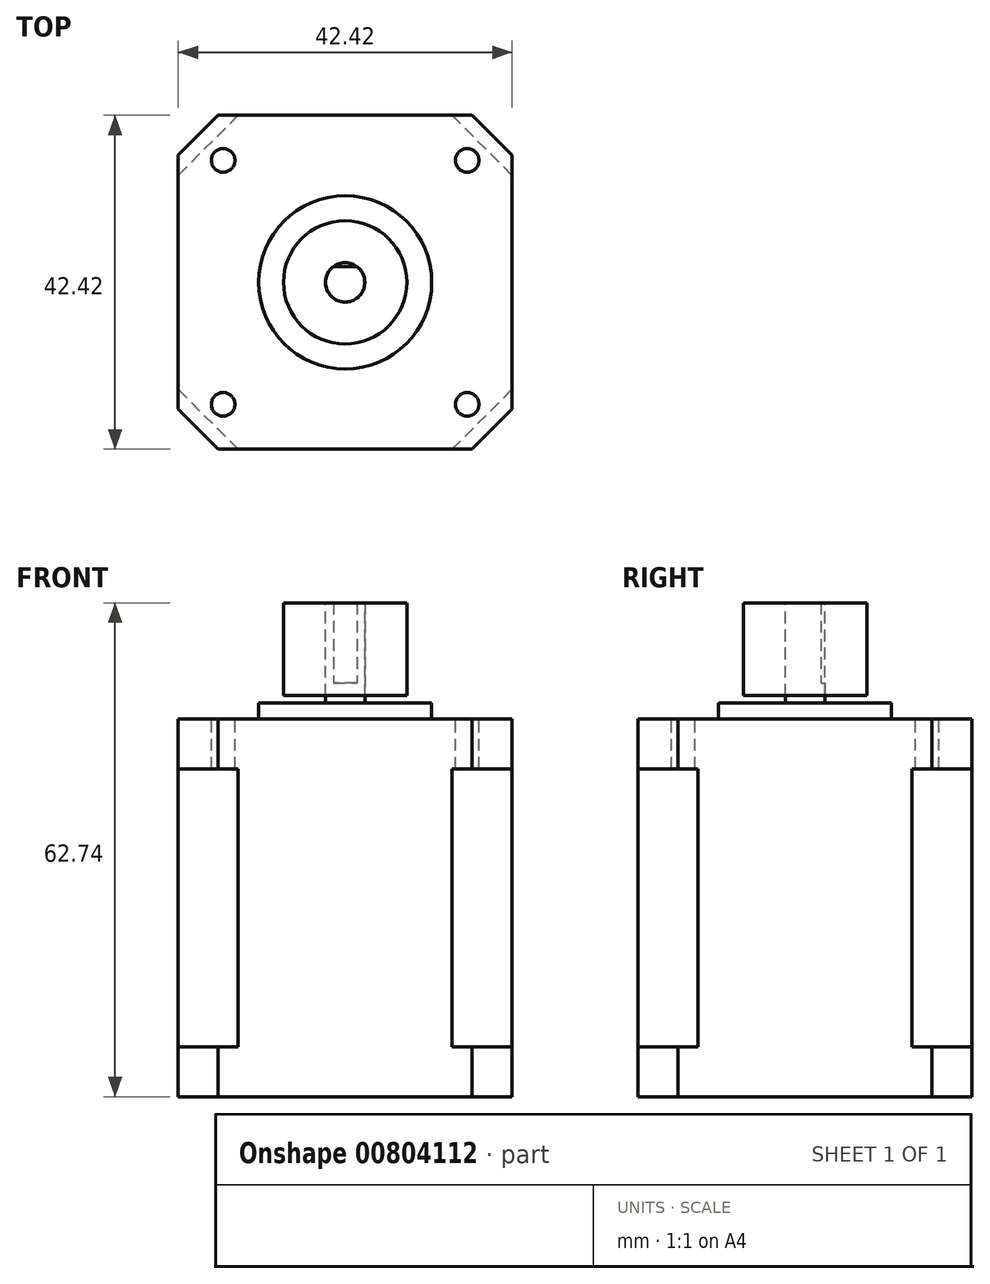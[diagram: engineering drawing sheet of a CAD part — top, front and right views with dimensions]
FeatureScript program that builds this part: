
annotation { "Feature Type Name" : "Feature", "Feature Type Description" : "" }
export const myFeature = defineFeature(function(context is Context, id is Id, definition is map)
    precondition{}
    {
        {
            var Q0;
            Q0=qCreatedBy(makeId("Top.planeOp"),FACE);
            var sketch = newSketch(context, id + "F0", { "sketchPlane" : qUnion([Q0]), "asVersion" : FeatureScriptVersionNumber.V236_DEFAULT_MAX_ASSEMBLIES});
            skLineSegment(sketch, "E0.bottom", {"start": v(-21.2, 21.2) * mm, "end": v(21.2, 21.2) * mm});
            skLineSegment(sketch, "E0.top", {"start": v(-21.2, -21.2) * mm, "end": v(21.2, -21.2) * mm});
            skLineSegment(sketch, "E0.left", {"start": v(-21.2, 21.2) * mm, "end": v(-21.2, -21.2) * mm});
            skLineSegment(sketch, "E0.right", {"start": v(21.2, 21.2) * mm, "end": v(21.2, -21.2) * mm});
            skSolve(sketch);
        }
        {
            var Q0;
            Q0=makeQuery(id+"F0.imprint","IMPRINT",FACE,{"disambiguationData":[TD([[makeQuery(id+"F0.imprint","IMPRINT",EDGE,{"derivedFrom":sQuery(id+"F0.wireOp",EDGE,"E0.bottom")}),-1.0]])]});
            extrude(context, id + "F1", {"entities" : qUnion([Q0]), "endBound" : BoundingType.SYMMETRIC, "depth" : 35.3 * mm});
        }
        {
            var Q0;
            Q0=makeQuery(id+"F1.opExtrude","SWEPT_EDGE",EDGE,{"disambiguationData":[OSD([sQuery(id+"F0.wireOp",EDGE,"E0.bottom"),sQuery(id+"F0.wireOp",EDGE,"E0.right")])]});
            var Q1;
            Q1=makeQuery(id+"F1.opExtrude","SWEPT_EDGE",EDGE,{"disambiguationData":[OSD([sQuery(id+"F0.wireOp",EDGE,"E0.bottom"),sQuery(id+"F0.wireOp",EDGE,"E0.left")])]});
            var Q2;
            Q2=makeQuery(id+"F1.opExtrude","SWEPT_EDGE",EDGE,{"disambiguationData":[OSD([sQuery(id+"F0.wireOp",EDGE,"E0.top"),sQuery(id+"F0.wireOp",EDGE,"E0.left")])]});
            var Q3;
            Q3=makeQuery(id+"F1.opExtrude","SWEPT_EDGE",EDGE,{"disambiguationData":[OSD([sQuery(id+"F0.wireOp",EDGE,"E0.top"),sQuery(id+"F0.wireOp",EDGE,"E0.right")])]});
            chamfer(context, id + "F2", {"entities" : qUnion([Q0, Q1, Q2, Q3]), "width" : 7.62 * mm, "tangentPropagation" : true});
        }
        {
            var Q0;
            Q0=makeQuery(id+"F1.opExtrude","CAP_FACE",FACE,{"disambiguationData":[OSD([sQuery(id+"F0.wireOp",EDGE,"E0.bottom"),sQuery(id+"F0.wireOp",EDGE,"E0.top"),sQuery(id+"F0.wireOp",EDGE,"E0.left"),sQuery(id+"F0.wireOp",EDGE,"E0.right")])],"isStart":false});
            var sketch = newSketch(context, id + "F3", { "sketchPlane" : qUnion([Q0]), "asVersion" : FeatureScriptVersionNumber.V236_DEFAULT_MAX_ASSEMBLIES});
            skLineSegment(sketch, "E1.bottom", {"start": v(-21.2, 21.2) * mm, "end": v(21.2, 21.2) * mm});
            skLineSegment(sketch, "E1.top", {"start": v(-21.2, -21.2) * mm, "end": v(21.2, -21.2) * mm});
            skLineSegment(sketch, "E1.left", {"start": v(-21.2, 21.2) * mm, "end": v(-21.2, -21.2) * mm});
            skLineSegment(sketch, "E1.right", {"start": v(21.2, 21.2) * mm, "end": v(21.2, -21.2) * mm});
            skSolve(sketch);
        }
        {
            var Q0;
            {var subQ0=sQuery(id+"F0.wireOp",EDGE,"E0.top");var subQ1=sQuery(id+"F0.wireOp",EDGE,"E0.right");var subQ2=sQuery(id+"F0.wireOp",EDGE,"E0.bottom");var subQ3=sQuery(id+"F0.wireOp",EDGE,"E0.left");var subQ4=makeQuery(id+"F1.opExtrude","CAP_FACE",FACE,{"disambiguationData":[OSD([subQ2,subQ0,subQ3,subQ1])],"isStart":false});var subQ8=makeQuery(id+"F2.opChamfer","BLEND_EDGE",EDGE,{"blendedFrom":[makeQuery(id+"F1.opExtrude","SWEPT_EDGE",EDGE,{"disambiguationData":[OSD([subQ2,subQ3])]}),subQ4],"blendedInto":[subQ4]});Q0=makeQuery(id+"F3.imprint","IMPRINT",FACE,{"disambiguationData":[TD([[makeQuery(id+"F3.imprint","IMPRINT",EDGE,{"derivedFrom":subQ8}),1.0]])]});}
            var Q1;
            {var subQ0=sQuery(id+"F0.wireOp",EDGE,"E0.bottom");var subQ1=sQuery(id+"F0.wireOp",EDGE,"E0.right");var subQ2=makeQuery(id+"F2.opChamfer","BLEND_EDGE",EDGE,{"blendedFrom":[makeQuery(id+"F1.opExtrude","SWEPT_EDGE",EDGE,{"disambiguationData":[OSD([subQ0,subQ1])]}),makeQuery(id+"F1.opExtrude","CAP_FACE",FACE,{"disambiguationData":[OSD([subQ0,sQuery(id+"F0.wireOp",EDGE,"E0.top"),sQuery(id+"F0.wireOp",EDGE,"E0.left"),subQ1])],"isStart":false})],"blendedInto":[makeQuery(id+"F1.opExtrude","CAP_FACE",FACE,{"disambiguationData":[OSD([subQ0,sQuery(id+"F0.wireOp",EDGE,"E0.top"),sQuery(id+"F0.wireOp",EDGE,"E0.left"),subQ1])],"isStart":false})]});Q1=makeQuery(id+"F3.imprint","IMPRINT",FACE,{"disambiguationData":[TD([[makeQuery(id+"F3.imprint","IMPRINT",EDGE,{"derivedFrom":subQ2}),-1.0]])]});}
            var Q2;
            {var subQ0=sQuery(id+"F0.wireOp",EDGE,"E0.bottom");var subQ1=sQuery(id+"F0.wireOp",EDGE,"E0.left");var subQ2=makeQuery(id+"F2.opChamfer","BLEND_EDGE",EDGE,{"blendedFrom":[makeQuery(id+"F1.opExtrude","SWEPT_EDGE",EDGE,{"disambiguationData":[OSD([subQ0,subQ1])]}),makeQuery(id+"F1.opExtrude","CAP_FACE",FACE,{"disambiguationData":[OSD([subQ0,sQuery(id+"F0.wireOp",EDGE,"E0.top"),subQ1,sQuery(id+"F0.wireOp",EDGE,"E0.right")])],"isStart":false})],"blendedInto":[makeQuery(id+"F1.opExtrude","CAP_FACE",FACE,{"disambiguationData":[OSD([subQ0,sQuery(id+"F0.wireOp",EDGE,"E0.top"),subQ1,sQuery(id+"F0.wireOp",EDGE,"E0.right")])],"isStart":false})]});Q2=makeQuery(id+"F3.imprint","IMPRINT",FACE,{"disambiguationData":[TD([[makeQuery(id+"F3.imprint","IMPRINT",EDGE,{"derivedFrom":subQ2}),-1.0]])]});}
            var Q3;
            {var subQ0=sQuery(id+"F0.wireOp",EDGE,"E0.top");var subQ1=sQuery(id+"F0.wireOp",EDGE,"E0.left");var subQ2=makeQuery(id+"F2.opChamfer","BLEND_EDGE",EDGE,{"blendedFrom":[makeQuery(id+"F1.opExtrude","SWEPT_EDGE",EDGE,{"disambiguationData":[OSD([subQ0,subQ1])]}),makeQuery(id+"F1.opExtrude","CAP_FACE",FACE,{"disambiguationData":[OSD([sQuery(id+"F0.wireOp",EDGE,"E0.bottom"),subQ0,subQ1,sQuery(id+"F0.wireOp",EDGE,"E0.right")])],"isStart":false})],"blendedInto":[makeQuery(id+"F1.opExtrude","CAP_FACE",FACE,{"disambiguationData":[OSD([sQuery(id+"F0.wireOp",EDGE,"E0.bottom"),subQ0,subQ1,sQuery(id+"F0.wireOp",EDGE,"E0.right")])],"isStart":false})]});Q3=makeQuery(id+"F3.imprint","IMPRINT",FACE,{"disambiguationData":[TD([[makeQuery(id+"F3.imprint","IMPRINT",EDGE,{"derivedFrom":subQ2}),-1.0]])]});}
            var Q4;
            {var subQ0=sQuery(id+"F0.wireOp",EDGE,"E0.top");var subQ1=sQuery(id+"F0.wireOp",EDGE,"E0.right");var subQ2=makeQuery(id+"F2.opChamfer","BLEND_EDGE",EDGE,{"blendedFrom":[makeQuery(id+"F1.opExtrude","SWEPT_EDGE",EDGE,{"disambiguationData":[OSD([subQ0,subQ1])]}),makeQuery(id+"F1.opExtrude","CAP_FACE",FACE,{"disambiguationData":[OSD([sQuery(id+"F0.wireOp",EDGE,"E0.bottom"),subQ0,sQuery(id+"F0.wireOp",EDGE,"E0.left"),subQ1])],"isStart":false})],"blendedInto":[makeQuery(id+"F1.opExtrude","CAP_FACE",FACE,{"disambiguationData":[OSD([sQuery(id+"F0.wireOp",EDGE,"E0.bottom"),subQ0,sQuery(id+"F0.wireOp",EDGE,"E0.left"),subQ1])],"isStart":false})]});Q4=makeQuery(id+"F3.imprint","IMPRINT",FACE,{"disambiguationData":[TD([[makeQuery(id+"F3.imprint","IMPRINT",EDGE,{"derivedFrom":subQ2}),-1.0]])]});}
            extrude(context, id + "F4", {"entities" : qUnion([Q0, Q1, Q2, Q3, Q4]), "operationType" : NewBodyOperationType.ADD, "depth" : 6.35 * mm});
        }
        {
            var Q0;
            Q0=makeQuery(id+"F4.opExtrude","SWEPT_EDGE",EDGE,{"disambiguationData":[OSD([sQuery(id+"F3.wireOp",EDGE,"E1.bottom"),sQuery(id+"F3.wireOp",EDGE,"E1.right")])]});
            var Q1;
            Q1=makeQuery(id+"F4.opExtrude","SWEPT_EDGE",EDGE,{"disambiguationData":[OSD([sQuery(id+"F3.wireOp",EDGE,"E1.bottom"),sQuery(id+"F3.wireOp",EDGE,"E1.left")])]});
            var Q2;
            Q2=makeQuery(id+"F4.opExtrude","SWEPT_EDGE",EDGE,{"disambiguationData":[OSD([sQuery(id+"F3.wireOp",EDGE,"E1.top"),sQuery(id+"F3.wireOp",EDGE,"E1.left")])]});
            var Q3;
            Q3=makeQuery(id+"F4.opExtrude","SWEPT_EDGE",EDGE,{"disambiguationData":[OSD([sQuery(id+"F3.wireOp",EDGE,"E1.top"),sQuery(id+"F3.wireOp",EDGE,"E1.right")])]});
            chamfer(context, id + "F5", {"entities" : qUnion([Q0, Q1, Q2, Q3]), "width" : 5.08 * mm, "tangentPropagation" : true});
        }
        {
            var Q0;
            Q0=makeQuery(id+"F1.opExtrude","CAP_FACE",FACE,{"disambiguationData":[OSD([sQuery(id+"F0.wireOp",EDGE,"E0.bottom"),sQuery(id+"F0.wireOp",EDGE,"E0.top"),sQuery(id+"F0.wireOp",EDGE,"E0.left"),sQuery(id+"F0.wireOp",EDGE,"E0.right")])],"isStart":true});
            var sketch = newSketch(context, id + "F6", { "sketchPlane" : qUnion([Q0]), "asVersion" : FeatureScriptVersionNumber.V236_DEFAULT_MAX_ASSEMBLIES});
            skLineSegment(sketch, "E2.0.0", {"start": v(-16.13, 21.2) * mm, "end": v(16.13, 21.2) * mm});
            skLineSegment(sketch, "E2.0.1", {"start": v(16.13, 21.2) * mm, "end": v(21.2, 16.13) * mm});
            skLineSegment(sketch, "E2.0.2", {"start": v(21.2, -16.13) * mm, "end": v(21.2, 16.13) * mm});
            skLineSegment(sketch, "E2.0.3", {"start": v(21.2, -16.13) * mm, "end": v(16.13, -21.2) * mm});
            skLineSegment(sketch, "E2.0.4", {"start": v(-16.13, -21.2) * mm, "end": v(16.13, -21.2) * mm});
            skLineSegment(sketch, "E2.0.5", {"start": v(-16.13, -21.2) * mm, "end": v(-21.2, -16.13) * mm});
            skLineSegment(sketch, "E2.0.6", {"start": v(-21.2, -16.13) * mm, "end": v(-21.2, 16.13) * mm});
            skLineSegment(sketch, "E2.0.7", {"start": v(-21.2, 16.13) * mm, "end": v(-16.13, 21.2) * mm});
            skSolve(sketch);
        }
        {
            var Q0;
            {var subQ3=sQuery(id+"F6.wireOp",EDGE,"E2.0.7");Q0=makeQuery(id+"F6.imprint","IMPRINT",FACE,{"disambiguationData":[TD([[makeQuery(id+"F6.imprint","IMPRINT",EDGE,{"derivedFrom":subQ3}),-1.0]])]});}
            var Q1;
            {var subQ4=sQuery(id+"F6.wireOp",EDGE,"E2.0.1");Q1=makeQuery(id+"F6.imprint","IMPRINT",FACE,{"disambiguationData":[TD([[makeQuery(id+"F6.imprint","IMPRINT",EDGE,{"derivedFrom":subQ4}),-1.0]])]});}
            var Q2;
            {var subQ4=sQuery(id+"F6.wireOp",EDGE,"E2.0.3");Q2=makeQuery(id+"F6.imprint","IMPRINT",FACE,{"disambiguationData":[TD([[makeQuery(id+"F6.imprint","IMPRINT",EDGE,{"derivedFrom":subQ4}),-1.0]])]});}
            var Q3;
            {var subQ4=sQuery(id+"F6.wireOp",EDGE,"E2.0.5");Q3=makeQuery(id+"F6.imprint","IMPRINT",FACE,{"disambiguationData":[TD([[makeQuery(id+"F6.imprint","IMPRINT",EDGE,{"derivedFrom":subQ4}),-1.0]])]});}
            var Q4;
            {var subQ0=sQuery(id+"F0.wireOp",EDGE,"E0.top");var subQ1=sQuery(id+"F0.wireOp",EDGE,"E0.right");var subQ2=sQuery(id+"F0.wireOp",EDGE,"E0.bottom");var subQ3=sQuery(id+"F0.wireOp",EDGE,"E0.left");var subQ4=makeQuery(id+"F1.opExtrude","CAP_FACE",FACE,{"disambiguationData":[OSD([subQ2,subQ0,subQ3,subQ1])],"isStart":true});var subQ8=makeQuery(id+"F2.opChamfer","BLEND_EDGE",EDGE,{"blendedFrom":[makeQuery(id+"F1.opExtrude","SWEPT_EDGE",EDGE,{"disambiguationData":[OSD([subQ2,subQ3])]}),subQ4],"blendedInto":[subQ4]});Q4=makeQuery(id+"F6.imprint","IMPRINT",FACE,{"disambiguationData":[TD([[makeQuery(id+"F6.imprint","IMPRINT",EDGE,{"derivedFrom":subQ8}),1.0]])]});}
            extrude(context, id + "F7", {"entities" : qUnion([Q0, Q1, Q2, Q3, Q4]), "operationType" : NewBodyOperationType.ADD, "depth" : 6.35 * mm});
        }
        {
            var Q0;
            Q0=makeQuery(id+"F4.opExtrude","CAP_FACE",FACE,{"disambiguationData":[OSD([sQuery(id+"F3.wireOp",EDGE,"E1.bottom"),sQuery(id+"F3.wireOp",EDGE,"E1.top"),sQuery(id+"F3.wireOp",EDGE,"E1.left"),sQuery(id+"F3.wireOp",EDGE,"E1.right")])],"isStart":false});
            var sketch = newSketch(context, id + "F8", { "sketchPlane" : qUnion([Q0]), "asVersion" : FeatureScriptVersionNumber.V236_DEFAULT_MAX_ASSEMBLIES});
            skCircle(sketch, "E3", {"center": v(0, 0) * mm, "radius": 11 * mm});
            skSolve(sketch);
        }
        {
            var Q0;
            Q0=makeQuery(id+"F8.imprint","IMPRINT",FACE,{"disambiguationData":[TD([[makeQuery(id+"F8.imprint","IMPRINT",EDGE,{"derivedFrom":sQuery(id+"F8.wireOp",EDGE,"E3")}),1.0]])]});
            extrude(context, id + "F9", {"entities" : qUnion([Q0]), "operationType" : NewBodyOperationType.ADD, "depth" : 2.03 * mm});
        }
        {
            var Q0;
            Q0=makeQuery(id+"F9.opExtrude","CAP_FACE",FACE,{"disambiguationData":[OSD([sQuery(id+"F8.wireOp",EDGE,"E3")])],"isStart":false});
            var sketch = newSketch(context, id + "F10", { "sketchPlane" : qUnion([Q0]), "asVersion" : FeatureScriptVersionNumber.V236_DEFAULT_MAX_ASSEMBLIES});
            skCircle(sketch, "E4", {"center": v(0, 0) * mm, "radius": 2.5 * mm});
            skSolve(sketch);
        }
        {
            var Q0;
            Q0=makeQuery(id+"F10.imprint","IMPRINT",FACE,{"disambiguationData":[TD([[makeQuery(id+"F10.imprint","IMPRINT",EDGE,{"derivedFrom":sQuery(id+"F10.wireOp",EDGE,"E4")}),1.0]])]});
            extrude(context, id + "F11", {"entities" : qUnion([Q0]), "operationType" : NewBodyOperationType.ADD, "depth" : 12.7 * mm});
        }
        {
            var Q0;
            Q0=makeQuery(id+"F11.opExtrude","CAP_FACE",FACE,{"disambiguationData":[OSD([sQuery(id+"F10.wireOp",EDGE,"E4")])],"isStart":false});
            var sketch = newSketch(context, id + "F12", { "sketchPlane" : qUnion([Q0]), "asVersion" : FeatureScriptVersionNumber.V236_DEFAULT_MAX_ASSEMBLIES});
            skLineSegment(sketch, "E5.bottom", {"start": v(-2.63, 2.93) * mm, "end": v(2.62, 2.93) * mm});
            skLineSegment(sketch, "E5.top", {"start": v(-2.63, 2) * mm, "end": v(2.62, 2) * mm});
            skLineSegment(sketch, "E5.left", {"start": v(-2.63, 2.93) * mm, "end": v(-2.63, 2) * mm});
            skLineSegment(sketch, "E5.right", {"start": v(2.62, 2.93) * mm, "end": v(2.62, 2) * mm});
            skSolve(sketch);
        }
        {
            var Q0;
            {var subQ0=makeQuery(id+"F11.opExtrude","CAP_EDGE",EDGE,{"disambiguationData":[OSD([sQuery(id+"F10.wireOp",EDGE,"E4")])],"isStart":false});var subQ1=sQuery(id+"F12.wireOp",EDGE,"E5.top");var subQ3=makeQuery(id+"F12.imprint","INTERSECT",VERTEX,{"disambiguationData":[OD(0.0)],"derivedFrom":[subQ0,subQ1]});Q0=qUnion([makeQuery(id+"F12.imprint","IMPRINT",FACE,{"disambiguationData":[TD([[makeQuery(id+"F12.imprint","IMPRINT",EDGE,{"derivedFrom":sQuery(id+"F12.wireOp",EDGE,"E5.bottom")}),-1.0]])]}),makeQuery(id+"F12.imprint","IMPRINT",FACE,{"disambiguationData":[TD([[makeQuery(id+"F12.imprint","IMPRINT",EDGE,{"disambiguationData":[TD([[subQ3,-1.0]])],"derivedFrom":subQ1}),1.0]])]})]);}
            extrude(context, id + "F13", {"entities" : qUnion([Q0]), "operationType" : NewBodyOperationType.REMOVE, "oppositeDirection" : true, "depth" : 10.16 * mm});
        }
        {
            var Q0;
            Q0=makeQuery(id+"F4.opExtrude","CAP_FACE",FACE,{"disambiguationData":[OSD([sQuery(id+"F3.wireOp",EDGE,"E1.bottom"),sQuery(id+"F3.wireOp",EDGE,"E1.top"),sQuery(id+"F3.wireOp",EDGE,"E1.left"),sQuery(id+"F3.wireOp",EDGE,"E1.right")])],"isStart":false});
            var sketch = newSketch(context, id + "F14", { "sketchPlane" : qUnion([Q0]), "asVersion" : FeatureScriptVersionNumber.V236_DEFAULT_MAX_ASSEMBLIES});
            skLineSegment(sketch, "E6.rect.bottom", {"start": v(15.5, 15.5) * mm, "end": v(-15.5, 15.5) * mm, "construction": true});
            skLineSegment(sketch, "E6.rect.top", {"start": v(15.5, -15.5) * mm, "end": v(-15.5, -15.5) * mm, "construction": true});
            skLineSegment(sketch, "E6.rect.left", {"start": v(15.5, 15.5) * mm, "end": v(15.5, -15.5) * mm, "construction": true});
            skLineSegment(sketch, "E6.rect.right", {"start": v(-15.5, 15.5) * mm, "end": v(-15.5, -15.5) * mm, "construction": true});
            skPoint(sketch, "E6.rect.middle", {"position": v(0, 0) * mm});
            skCircle(sketch, "E7", {"center": v(-15.5, 15.5) * mm, "radius": 1.5 * mm});
            skCircle(sketch, "E8", {"center": v(15.5, 15.5) * mm, "radius": 1.5 * mm});
            skCircle(sketch, "E9", {"center": v(15.5, -15.5) * mm, "radius": 1.5 * mm});
            skCircle(sketch, "E10", {"center": v(-15.5, -15.5) * mm, "radius": 1.5 * mm});
            skSolve(sketch);
        }
        {
            var Q0;
            Q0=makeQuery(id+"F14.imprint","IMPRINT",FACE,{"disambiguationData":[TD([[makeQuery(id+"F14.imprint","IMPRINT",EDGE,{"derivedFrom":sQuery(id+"F14.wireOp",EDGE,"E7")}),1.0]])]});
            var Q1;
            Q1=makeQuery(id+"F14.imprint","IMPRINT",FACE,{"disambiguationData":[TD([[makeQuery(id+"F14.imprint","IMPRINT",EDGE,{"derivedFrom":sQuery(id+"F14.wireOp",EDGE,"E8")}),1.0]])]});
            var Q2;
            Q2=makeQuery(id+"F14.imprint","IMPRINT",FACE,{"disambiguationData":[TD([[makeQuery(id+"F14.imprint","IMPRINT",EDGE,{"derivedFrom":sQuery(id+"F14.wireOp",EDGE,"E9")}),1.0]])]});
            var Q3;
            Q3=makeQuery(id+"F14.imprint","IMPRINT",FACE,{"disambiguationData":[TD([[makeQuery(id+"F14.imprint","IMPRINT",EDGE,{"derivedFrom":sQuery(id+"F14.wireOp",EDGE,"E10")}),1.0]])]});
            extrude(context, id + "F15", {"entities" : qUnion([Q0, Q1, Q2, Q3]), "operationType" : NewBodyOperationType.REMOVE, "oppositeDirection" : true, "depth" : 6.35 * mm});
        }
        {
            var Q0;
            Q0=makeQuery(id+"F11.opExtrude","CAP_FACE",FACE,{"disambiguationData":[OSD([sQuery(id+"F10.wireOp",EDGE,"E4")])],"isStart":false});
            var sketch = newSketch(context, id + "F16", { "sketchPlane" : qUnion([Q0]), "asVersion" : FeatureScriptVersionNumber.V236_DEFAULT_MAX_ASSEMBLIES});
            skCircle(sketch, "E11", {"center": v(0, 0) * mm, "radius": 7.83 * mm});
            skCircle(sketch, "E12", {"center": v(0, 0) * mm, "radius": 2.5 * mm});
            skSolve(sketch);
        }
        {
            var Q0;
            Q0=makeQuery(id+"F16.imprint","IMPRINT",FACE,{"disambiguationData":[TD([[makeQuery(id+"F16.imprint","IMPRINT",EDGE,{"derivedFrom":sQuery(id+"F16.wireOp",EDGE,"E11")}),1.0]])]});
            extrude(context, id + "F17", {"entities" : qUnion([Q0]), "oppositeDirection" : true, "depth" : 11.8 * mm});
        }
    });
